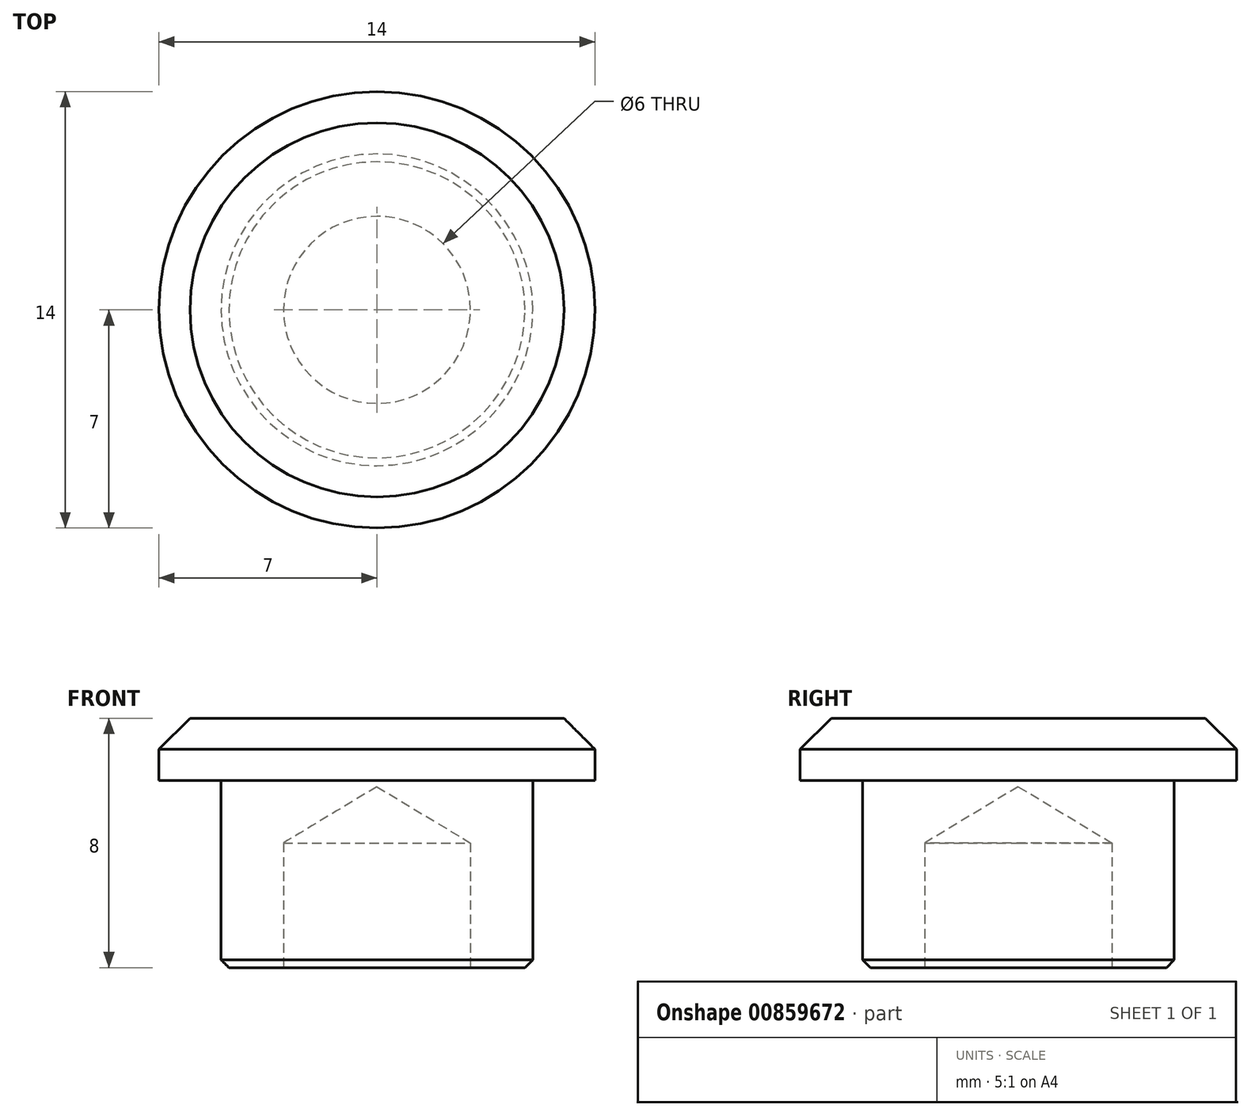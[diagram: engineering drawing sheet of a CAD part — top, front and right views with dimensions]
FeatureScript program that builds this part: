
annotation { "Feature Type Name" : "Feature", "Feature Type Description" : "" }
export const myFeature = defineFeature(function(context is Context, id is Id, definition is map)
    precondition{}
    {
        {
            var Q0;
            Q0=qCreatedBy(makeId("Top.planeOp"),FACE);
            var sketch = newSketch(context, id + "F0", { "sketchPlane" : qUnion([Q0])});
            skCircle(sketch, "E0", {"center": v(0, 0) * mm, "radius": 7 * mm});
            skSolve(sketch);
        }
        {
            var Q0;
            Q0 = qSketchRegion(id + "F0", true);
            extrude(context, id + "F1", {"entities" : qUnion([Q0]), "depth" : 2 * mm, "offsetDistance" : 25 * mm});
        }
        {
            var Q0;
            Q0=makeQuery(id+"F1.opExtrude","CAP_FACE",FACE,{"disambiguationData":[OSD([sQuery(id+"F0.wireOp",EDGE,"E0")])],"isStart":false});
            chamfer(context, id + "F2", {"entities" : qUnion([Q0]), "width" : 1 * mm, "tangentPropagation" : true});
        }
        {
            var Q0;
            Q0=makeQuery(id+"F1.opExtrude","CAP_FACE",FACE,{"disambiguationData":[OSD([sQuery(id+"F0.wireOp",EDGE,"E0")])],"isStart":true});
            var sketch = newSketch(context, id + "F3", { "sketchPlane" : qUnion([Q0])});
            skCircle(sketch, "E1", {"center": v(0, 0) * mm, "radius": 5 * mm});
            skSolve(sketch);
        }
        {
            var Q0;
            Q0 = qSketchRegion(id + "F3", true);
            extrude(context, id + "F4", {"entities" : qUnion([Q0]), "operationType" : NewBodyOperationType.ADD, "depth" : 6 * mm, "offsetDistance" : 25 * mm});
        }
        {
            var Q0;
            Q0=makeQuery(id+"F4.opExtrude","CAP_EDGE",EDGE,{"disambiguationData":[OSD([sQuery(id+"F3.wireOp",EDGE,"E1")])],"isStart":false});
            chamfer(context, id + "F5", {"entities" : qUnion([Q0]), "width" : 0.25 * mm, "tangentPropagation" : true});
        }
        {
            var Q0;
            Q0=makeQuery(id+"F4.opExtrude","CAP_FACE",FACE,{"disambiguationData":[OSD([sQuery(id+"F3.wireOp",EDGE,"E1")])],"isStart":false});
            var sketch = newSketch(context, id + "F6", { "sketchPlane" : qUnion([Q0])});
            skPoint(sketch, "E2", {"position": v(0, 0) * mm});
            skSolve(sketch);
        }
        {
            var Q0;
            Q0=sQuery(id+"F6.wireOp",VERTEX,"E2");
            var Q1;
            Q1=makeQuery(id+"F1.opExtrude","SWEPT_BODY",BODY,{"disambiguationData":[OSD([sQuery(id+"F0.wireOp",EDGE,"E0")])]});
            hole(context, id + "F7", {"style" : HoleStyle.SIMPLE, "endStyle" : HoleEndStyle.BLIND, "holeDiameter" : 6 * mm, "majorDiameter" : 5 * mm, "holeDepth" : 4 * mm, "isTappedThrough" : true, "tappedDepth" : 12 * mm, "tapClearance" : 3, "locations" : qUnion([Q0]), "scope" : qUnion([Q1])});
        }
    });
